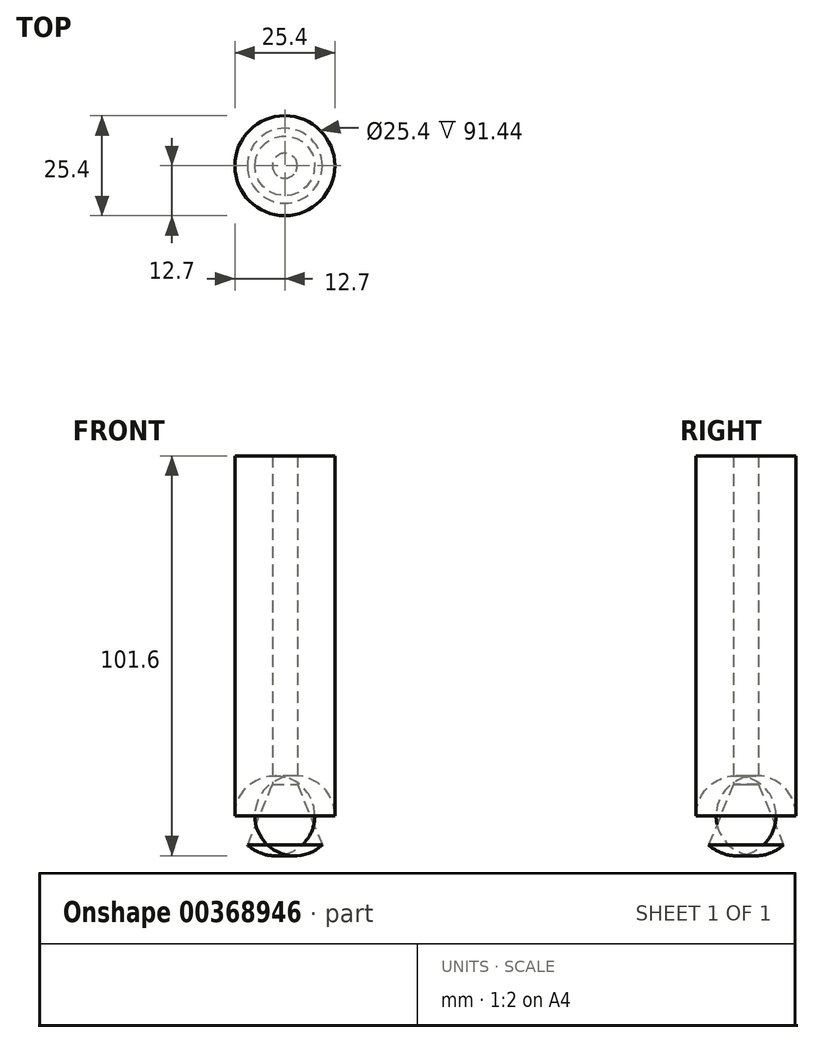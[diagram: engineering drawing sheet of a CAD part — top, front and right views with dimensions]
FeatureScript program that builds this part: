
annotation { "Feature Type Name" : "Feature", "Feature Type Description" : "" }
export const myFeature = defineFeature(function(context is Context, id is Id, definition is map)
    precondition{}
    {
        {
            var Q0;
            Q0=qCreatedBy(makeId("Top.planeOp"),FACE);
            var sketch = newSketch(context, id + "F0", { "sketchPlane" : qUnion([Q0])});
            skCircle(sketch, "E0", {"center": v(0, 0) * mm, "radius": 12.7 * mm});
            skSolve(sketch);
        }
        {
            var Q0;
            Q0 = qSketchRegion(id + "F0", true);
            extrude(context, id + "F1", {"entities" : qUnion([Q0]), "oppositeDirection" : true, "depth" : 101.6 * mm});
        }
        {
            var Q0;
            Q0=makeQuery(id+"F1.opExtrude","CAP_FACE",FACE,{"disambiguationData":[OSD([sQuery(id+"F0.wireOp",EDGE,"E0")])],"isStart":false});
            var sketch = newSketch(context, id + "F2", { "sketchPlane" : qUnion([Q0])});
            skCircle(sketch, "E1", {"center": v(0, 0) * mm, "radius": 3.18 * mm});
            skSolve(sketch);
        }
        {
            var Q0;
            Q0=makeQuery(id+"F1.opExtrude","CAP_EDGE",EDGE,{"disambiguationData":[OSD([sQuery(id+"F0.wireOp",EDGE,"E0")])],"isStart":false});
            fillet(context, id + "F3", {"entities" : qUnion([Q0]), "radius" : 10.16 * mm, "tangentPropagation" : true, "allowEdgeOverflow" : false});
        }
        {
            var Q0;
            Q0=sQuery(id+"F2.wireOp",VERTEX,"E1.center");
            var Q1;
            Q1=makeQuery(id+"F1.opExtrude","SWEPT_BODY",BODY,{"disambiguationData":[OSD([sQuery(id+"F0.wireOp",EDGE,"E0")])]});
            hole(context, id + "F4", {"style" : HoleStyle.C_SINK, "endStyle" : HoleEndStyle.THROUGH, "holeDiameter" : 6.35 * mm, "cSinkDiameter" : 19.05 * mm, "cSinkAngle" : 44.9 * degree, "isTappedThrough" : true, "tappedDepth" : 12.7 * mm, "tapClearance" : 3, "locations" : qUnion([Q0]), "scope" : qUnion([Q1])});
        }
    });
